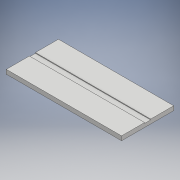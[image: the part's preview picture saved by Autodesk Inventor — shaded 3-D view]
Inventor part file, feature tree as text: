
AUTODESK INVENTOR PART (.ipt)
format: ipt  version: 2018.3 (Build 223284000, 284)  size: 105,472 bytes
history: native  units: mm
features: extrude x2, sketch x2
ambient origin geometry x8: Origin, YZ Plane, XZ Plane, XY Plane, X Axis, Y Axis, Z Axis, Center Point
bodies: Solid1 (feature_tree)
feature tree (4):
  extrude  "Extrusion1"  Depth=32.5mm
  extrude  "Extrusion2"  Depth=32.5mm
  sketch  "Sketch1"  dims[d0=14.7mm d1=32.5mm]
  sketch  "Sketch2"  dims[d2=1.2mm d3=0.0mm d4=32.5mm d5=1.7mm d6=6.5mm d7=0.2mm d8=0.0mm]
